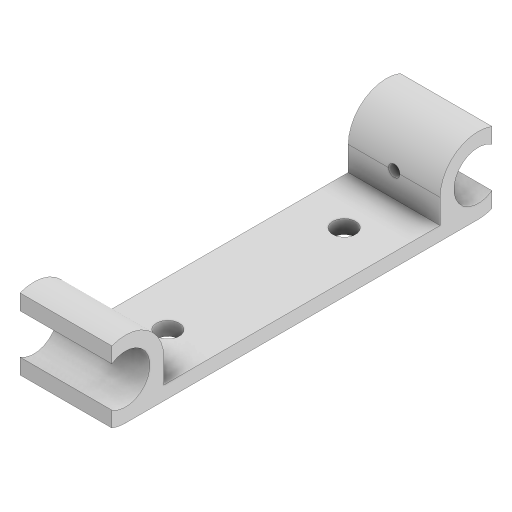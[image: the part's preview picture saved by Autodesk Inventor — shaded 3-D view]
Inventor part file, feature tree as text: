
AUTODESK INVENTOR PART (.ipt)
format: ipt  version: 2023 (Build 270158000, 158)  size: 182,272 bytes
history: native  units: mm
features: extrude x4, projected_geometry x4, sketch x3, other x2
ambient origin geometry x8: Origin, YZ Plane, XZ Plane, XY Plane, X Axis, Y Axis, Z Axis, Center Point
bodies: Body1 (feature_tree)
feature tree (13):
  other  "솔리드1"
  extrude  "돌출1"  Depth=10.6mm
  other  "작업 평면1"
  extrude  "돌출2"  Depth=3.0mm
  sketch  "스케치3"
  extrude  "돌출3"  Depth=10.0mm
  extrude  "돌출4"  Depth=16.6mm
  sketch  "스케치1"
  sketch  "스케치2"
  projected_geometry  "투영된 루프1"
  projected_geometry  "투영된 루프2"
  projected_geometry  "투영된 루프3"
  projected_geometry  "투영된 루프4"
